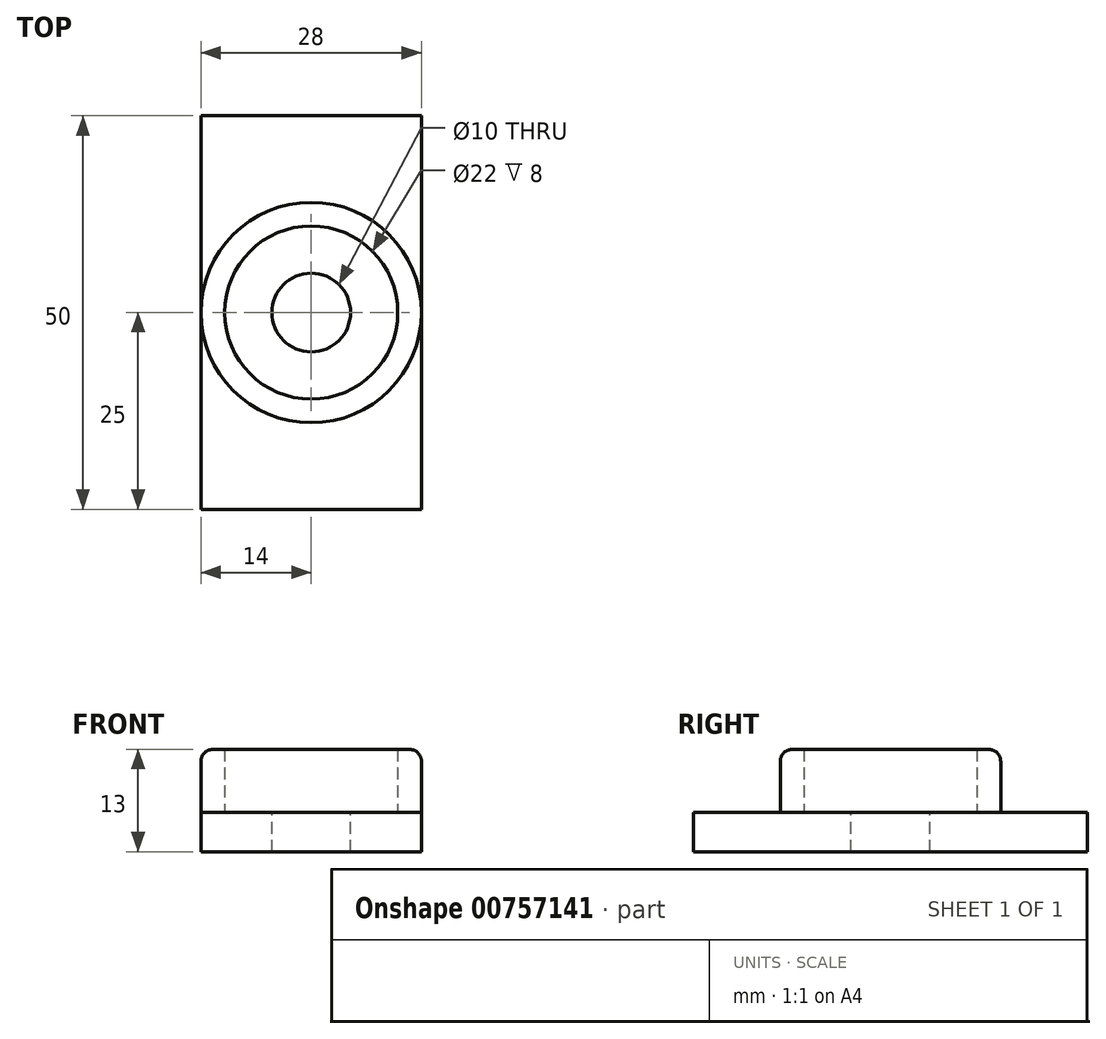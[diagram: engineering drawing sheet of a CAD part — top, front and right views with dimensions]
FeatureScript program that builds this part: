
annotation { "Feature Type Name" : "Feature", "Feature Type Description" : "" }
export const myFeature = defineFeature(function(context is Context, id is Id, definition is map)
    precondition{}
    {
        {
            var Q0;
            Q0=qCreatedBy(makeId("Top.planeOp"),FACE);
            var sketch = newSketch(context, id + "F0", { "sketchPlane" : qUnion([Q0])});
            skLineSegment(sketch, "E0.bottom", {"start": v(0, 0) * mm, "end": v(28, 0) * mm});
            skLineSegment(sketch, "E0.top", {"start": v(0, 50) * mm, "end": v(28, 50) * mm});
            skLineSegment(sketch, "E0.left", {"start": v(0, 0) * mm, "end": v(0, 50) * mm});
            skLineSegment(sketch, "E0.right", {"start": v(28, 0) * mm, "end": v(28, 50) * mm});
            skSolve(sketch);
        }
        {
            var Q0;
            Q0 = qSketchRegion(id + "F0", true);
            extrude(context, id + "F1", {"entities" : qUnion([Q0]), "depth" : 5 * mm, "offsetDistance" : 25 * mm});
        }
        {
            var Q0;
            Q0=makeQuery(id+"F1.opExtrude","CAP_FACE",FACE,{"disambiguationData":[OSD([sQuery(id+"F0.wireOp",EDGE,"E0.bottom"),sQuery(id+"F0.wireOp",EDGE,"E0.top"),sQuery(id+"F0.wireOp",EDGE,"E0.left"),sQuery(id+"F0.wireOp",EDGE,"E0.right")])],"isStart":false});
            var sketch = newSketch(context, id + "F2", { "sketchPlane" : qUnion([Q0])});
            skCircle(sketch, "E1", {"center": v(14, 25) * mm, "radius": 5 * mm});
            skPoint(sketch, "E2", {"position": v(0, 25) * mm});
            skPoint(sketch, "E3", {"position": v(14, 0) * mm});
            skLineSegment(sketch, "E4.top", {"start": v(0, 25) * mm, "end": v(14, 25) * mm, "construction": true});
            skLineSegment(sketch, "E4.right", {"start": v(14, 0) * mm, "end": v(14, 25) * mm, "construction": true});
            skSolve(sketch);
        }
        {
            var Q0;
            Q0 = qSketchRegion(id + "F2", true);
            var Q1;
            Q1=makeQuery(id+"F1.opExtrude","CAP_FACE",FACE,{"disambiguationData":[OSD([sQuery(id+"F0.wireOp",EDGE,"E0.bottom"),sQuery(id+"F0.wireOp",EDGE,"E0.top"),sQuery(id+"F0.wireOp",EDGE,"E0.left"),sQuery(id+"F0.wireOp",EDGE,"E0.right")])],"isStart":true});
            extrude(context, id + "F3", {"entities" : qUnion([Q0]), "operationType" : NewBodyOperationType.REMOVE, "endBound" : BoundingType.UP_TO_SURFACE, "oppositeDirection" : true, "depth" : 25 * mm, "endBoundEntityFace" : qUnion([Q1]), "offsetDistance" : 25 * mm});
        }
        {
            var Q0;
            Q0=makeQuery(id+"F1.opExtrude","CAP_FACE",FACE,{"disambiguationData":[OSD([sQuery(id+"F0.wireOp",EDGE,"E0.bottom"),sQuery(id+"F0.wireOp",EDGE,"E0.top"),sQuery(id+"F0.wireOp",EDGE,"E0.left"),sQuery(id+"F0.wireOp",EDGE,"E0.right")])],"isStart":false});
            var sketch = newSketch(context, id + "F4", { "sketchPlane" : qUnion([Q0])});
            skCircle(sketch, "E5", {"center": v(14, 25) * mm, "radius": 11 * mm});
            skCircle(sketch, "E6.0", {"center": v(14, 25) * mm, "radius": 14 * mm});
            skSolve(sketch);
        }
        {
            var Q0;
            Q0 = qSketchRegion(id + "F4", true);
            extrude(context, id + "F5", {"entities" : qUnion([Q0]), "operationType" : NewBodyOperationType.ADD, "depth" : 8 * mm, "offsetDistance" : 25 * mm});
        }
        {
            var Q0;
            Q0=makeQuery(id+"F5.opExtrude","CAP_EDGE",EDGE,{"disambiguationData":[OSD([sQuery(id+"F4.wireOp",EDGE,"E6.0")])],"isStart":false});
            fillet(context, id + "F6", {"entities" : qUnion([Q0]), "radius" : 1.5 * mm, "tangentPropagation" : true, "allowEdgeOverflow" : false});
        }
    });
